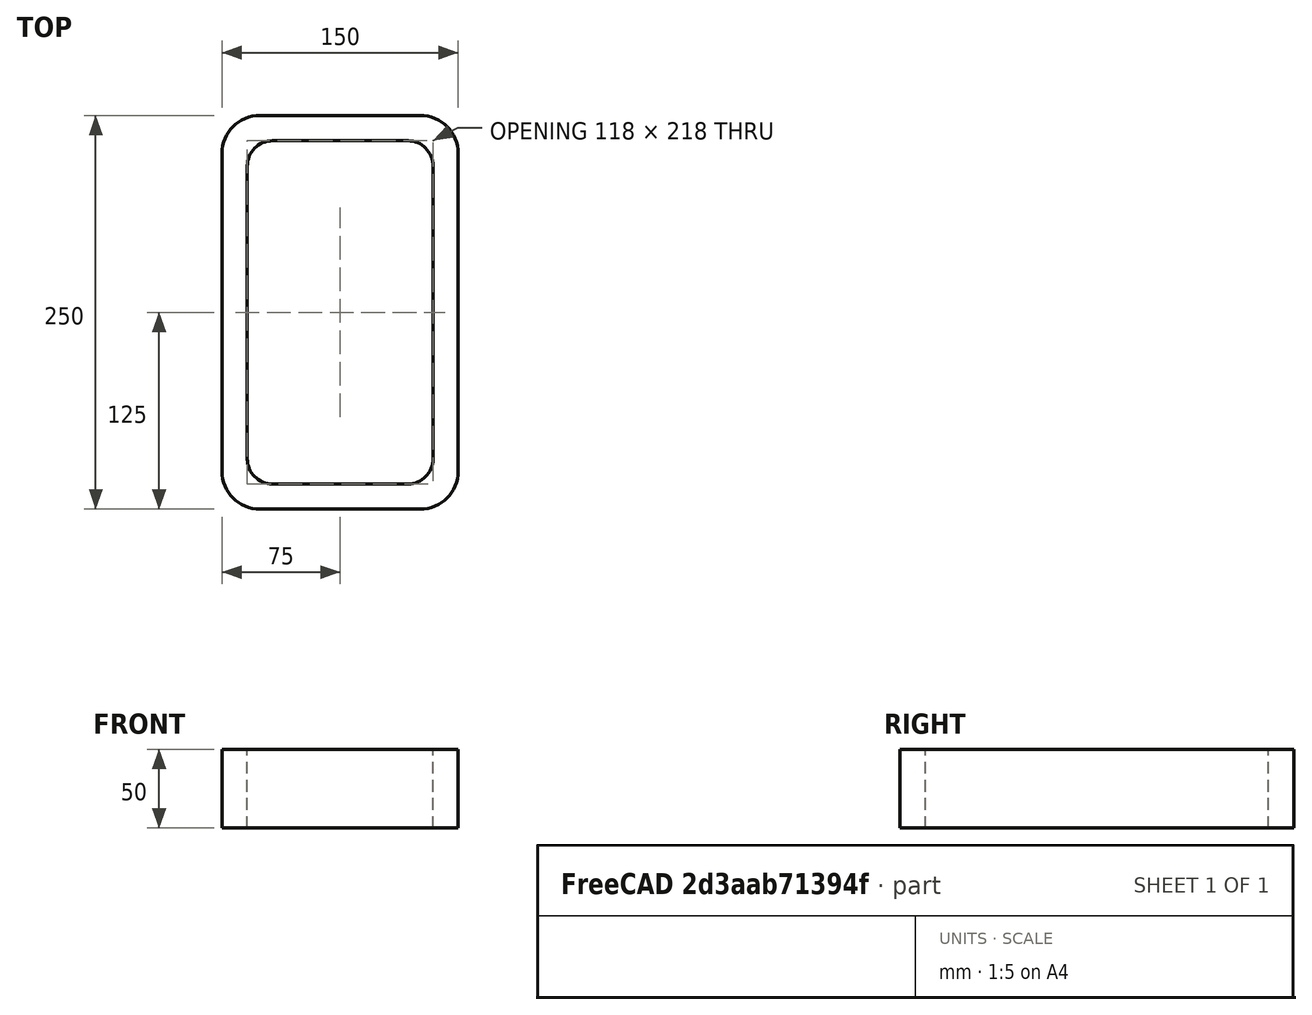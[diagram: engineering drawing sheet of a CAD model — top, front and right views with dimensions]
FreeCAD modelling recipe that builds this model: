
FCSTD DOCUMENT  (FreeCAD 0.15R4671 (Git))
Label: Rectangular hollow section 250x150x16 EN10219 S235JRH
License: All rights reserved
LicenseURL: http://en.wikipedia.org/wiki/All_rights_reserved
objects: Sketcher::SketchObject×1, Part::Extrusion×1
note: 2 computed .brp shape members not serialized (recipe doc carries the construction recipe); baked Part::Feature solids carry a one-line shape summary decoded from their .brp

FEATURE [Sketcher::SketchObject] Sketch
  sketch-geometry (16):
    g0: LineSegment StartX=-43 StartY=109 StartZ=0 EndX=43 EndY=109 EndZ=0
    g1: LineSegment StartX=59 StartY=93 StartZ=0 EndX=59 EndY=-93 EndZ=0
    g2: LineSegment StartX=43 StartY=-109 StartZ=0 EndX=-43 EndY=-109 EndZ=0
    g3: LineSegment StartX=-59 StartY=-93 StartZ=0 EndX=-59 EndY=93 EndZ=0
    g4: LineSegment StartX=-51 StartY=125 StartZ=0 EndX=51 EndY=125 EndZ=0
    g5: LineSegment StartX=75 StartY=101 StartZ=0 EndX=75 EndY=-101 EndZ=0
    g6: LineSegment StartX=51 StartY=-125 StartZ=0 EndX=-51 EndY=-125 EndZ=0
    g7: LineSegment StartX=-75 StartY=-101 StartZ=0 EndX=-75 EndY=101 EndZ=0
    g8: ArcOfCircle CenterX=-43 CenterY=93 CenterZ=0 NormalX=0 NormalY=0 NormalZ=1 Radius=16 StartAngle=1.5708 EndAngle=3.14159
    g9: ArcOfCircle CenterX=43 CenterY=93 CenterZ=0 NormalX=0 NormalY=0 NormalZ=1 Radius=16 StartAngle=0 EndAngle=1.5708
    g10: ArcOfCircle CenterX=43 CenterY=-93 CenterZ=0 NormalX=0 NormalY=0 NormalZ=1 Radius=16 StartAngle=4.71239 EndAngle=6.28319
    g11: ArcOfCircle CenterX=-43 CenterY=-93 CenterZ=0 NormalX=0 NormalY=0 NormalZ=1 Radius=16 StartAngle=3.14159 EndAngle=4.71239
    g12: ArcOfCircle CenterX=51 CenterY=101 CenterZ=0 NormalX=0 NormalY=0 NormalZ=1 Radius=24 StartAngle=0 EndAngle=1.5708
    g13: ArcOfCircle CenterX=51 CenterY=-101 CenterZ=0 NormalX=0 NormalY=0 NormalZ=1 Radius=24 StartAngle=4.71239 EndAngle=6.28319
    g14: ArcOfCircle CenterX=-51 CenterY=-101 CenterZ=0 NormalX=0 NormalY=0 NormalZ=1 Radius=24 StartAngle=3.14159 EndAngle=4.71239
    g15: ArcOfCircle CenterX=-51 CenterY=101 CenterZ=0 NormalX=0 NormalY=0 NormalZ=1 Radius=24 StartAngle=1.5708 EndAngle=3.14159
  constraints (36):
    c: Horizontal(g2)
    c: Vertical(g3)
    c: Horizontal(g6)
    c: Vertical(g7)
    c: Tangent(g3,g8) = 1.5708
    c: Tangent(g0,g8) = 1.5708
    c: Tangent(g0,g9) = 1.5708
    c: Tangent(g1,g9) = 1.5708
    c: Tangent(g1,g10) = 1.5708
    c: Tangent(g2,g10) = 1.5708
    c: Tangent(g2,g11) = 1.5708
    c: Tangent(g3,g11) = 1.5708
    c: Tangent(g4,g12) = 1.5708
    c: Tangent(g5,g12) = 1.5708
    c: Tangent(g5,g13) = 1.5708
    c: Tangent(g6,g13) = 1.5708
    c: Tangent(g6,g14) = 1.5708
    c: Tangent(g7,g14) = 1.5708
    c: Tangent(g7,g15) = 1.5708
    c: Tangent(g4,g15) = 1.5708
    c: Equal(g9,g8)
    c: Equal(g9,g11)
    c: Equal(g9,g10)
    c: Equal(g12,g15)
    c: Equal(g12,g14)
    c: Equal(g12,g13)
    c: Symmetric(g4,g6,g-1)
    c: Symmetric(g7,g5,g-2)
    c: DistanceY(g4,g6) = -250
    c: DistanceX(g7,g5) = 150
    c: Symmetric(g3,g1,g-2)
    c: Symmetric(g0,g2,g-1)
    c: DistanceY(g0,g4) = 16
    c: DistanceX(g5,g1) = -16
    c: Radius(g9) = 16
    c: Radius(g12) = 24
FEATURE [Part::Extrusion] Extrude  label="Rectangular hollow section 250x150x16 EN10219 S235JRH"
  Base = -> Sketch
  Dir = (0,0,50)
  Solid = true
